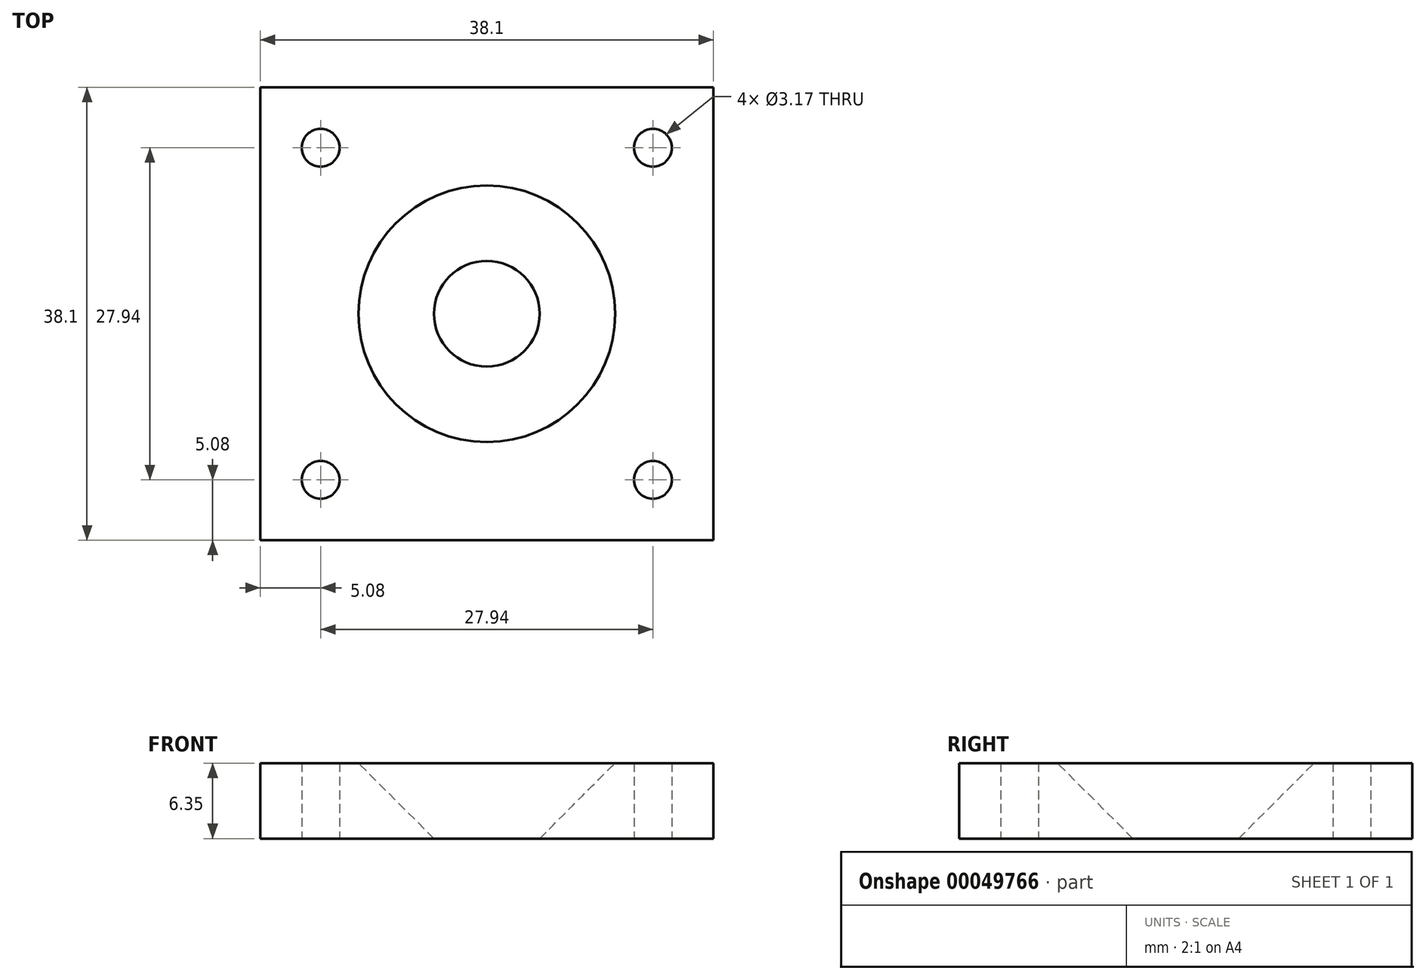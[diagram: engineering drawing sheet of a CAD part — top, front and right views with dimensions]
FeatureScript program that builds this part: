
annotation { "Feature Type Name" : "Feature", "Feature Type Description" : "" }
export const myFeature = defineFeature(function(context is Context, id is Id, definition is map)
    precondition{}
    {
        {
            var Q0;
            Q0=qCreatedBy(makeId("Top.planeOp"),FACE);
            var sketch = newSketch(context, id + "F0", { "sketchPlane" : qUnion([Q0])});
            skLineSegment(sketch, "E0.rect.bottom", {"start": v(19.05, -19.05) * mm, "end": v(-19.05, -19.05) * mm});
            skLineSegment(sketch, "E0.rect.top", {"start": v(19.05, 19.05) * mm, "end": v(-19.05, 19.05) * mm});
            skLineSegment(sketch, "E0.rect.left", {"start": v(19.05, -19.05) * mm, "end": v(19.05, 19.05) * mm});
            skLineSegment(sketch, "E0.rect.right", {"start": v(-19.05, -19.05) * mm, "end": v(-19.05, 19.05) * mm});
            skPoint(sketch, "E0.rect.middle", {"position": v(0, 0) * mm});
            skSolve(sketch);
        }
        {
            var Q0;
            Q0 = qSketchRegion(id + "F0", true);
            extrude(context, id + "F1", {"entities" : qUnion([Q0]), "depth" : 6.35 * mm});
        }
        {
            var Q0;
            Q0=qCreatedBy(makeId("Top.planeOp"),FACE);
            var sketch = newSketch(context, id + "F2", { "sketchPlane" : qUnion([Q0])});
            skCircle(sketch, "E1", {"center": v(0, 0) * mm, "radius": 4.45 * mm});
            skSolve(sketch);
        }
        {
            var Q0;
            Q0 = qSketchRegion(id + "F2", true);
            extrude(context, id + "F3", {"entities" : qUnion([Q0]), "operationType" : NewBodyOperationType.REMOVE, "depth" : 25.4 * mm});
        }
        {
            var Q0;
            Q0 = qSketchRegion(id + "F2", true);
            extrude(context, id + "F4", {"entities" : qUnion([Q0]), "operationType" : NewBodyOperationType.REMOVE, "depth" : 6.35 * mm, "hasDraft" : true, "draftAngle" : 45 * degree});
        }
        {
            var Q0;
            Q0=qCreatedBy(makeId("Top.planeOp"),FACE);
            var sketch = newSketch(context, id + "F5", { "sketchPlane" : qUnion([Q0])});
            skCircle(sketch, "E2", {"center": v(13.97, -13.97) * mm, "radius": 1.59 * mm});
            skCircle(sketch, "E3.MirrorC", {"center": v(13.97, 13.97) * mm, "radius": 1.59 * mm});
            skCircle(sketch, "E4.MirrorC", {"center": v(-13.97, -13.97) * mm, "radius": 1.59 * mm});
            skCircle(sketch, "E5.MirrorC", {"center": v(-13.97, 13.97) * mm, "radius": 1.59 * mm});
            skSolve(sketch);
        }
        {
            var Q0;
            Q0 = qSketchRegion(id + "F5", true);
            extrude(context, id + "F6", {"entities" : qUnion([Q0]), "operationType" : NewBodyOperationType.REMOVE, "depth" : 25.4 * mm});
        }
    });
